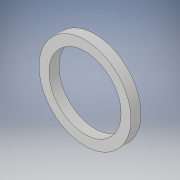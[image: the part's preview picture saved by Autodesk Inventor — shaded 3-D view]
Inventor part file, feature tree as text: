
AUTODESK INVENTOR PART (.ipt)
format: ipt  version: 2019 (Build 230136000, 136)  size: 103,936 bytes
history: native  units: mm
features: extrude x2, sketch x2
ambient origin geometry x8: Origin, YZ Plane, XZ Plane, XY Plane, X Axis, Y Axis, Z Axis, Center Point
bodies: Solid1 (feature_tree)
feature tree (4):
  extrude  "Extrusion1"  Depth=40.0mm TaperAngle=0.0deg
  extrude  "Extrusion2"  Depth=4.0mm TaperAngle=0.0deg
  sketch  "Sketch1"  dims[d0=370.0mm d1=40.0mm d2=0.0mm]
  sketch  "Sketch2"  dims[d3=290.0mm d4=4.0mm d5=0.0mm]
